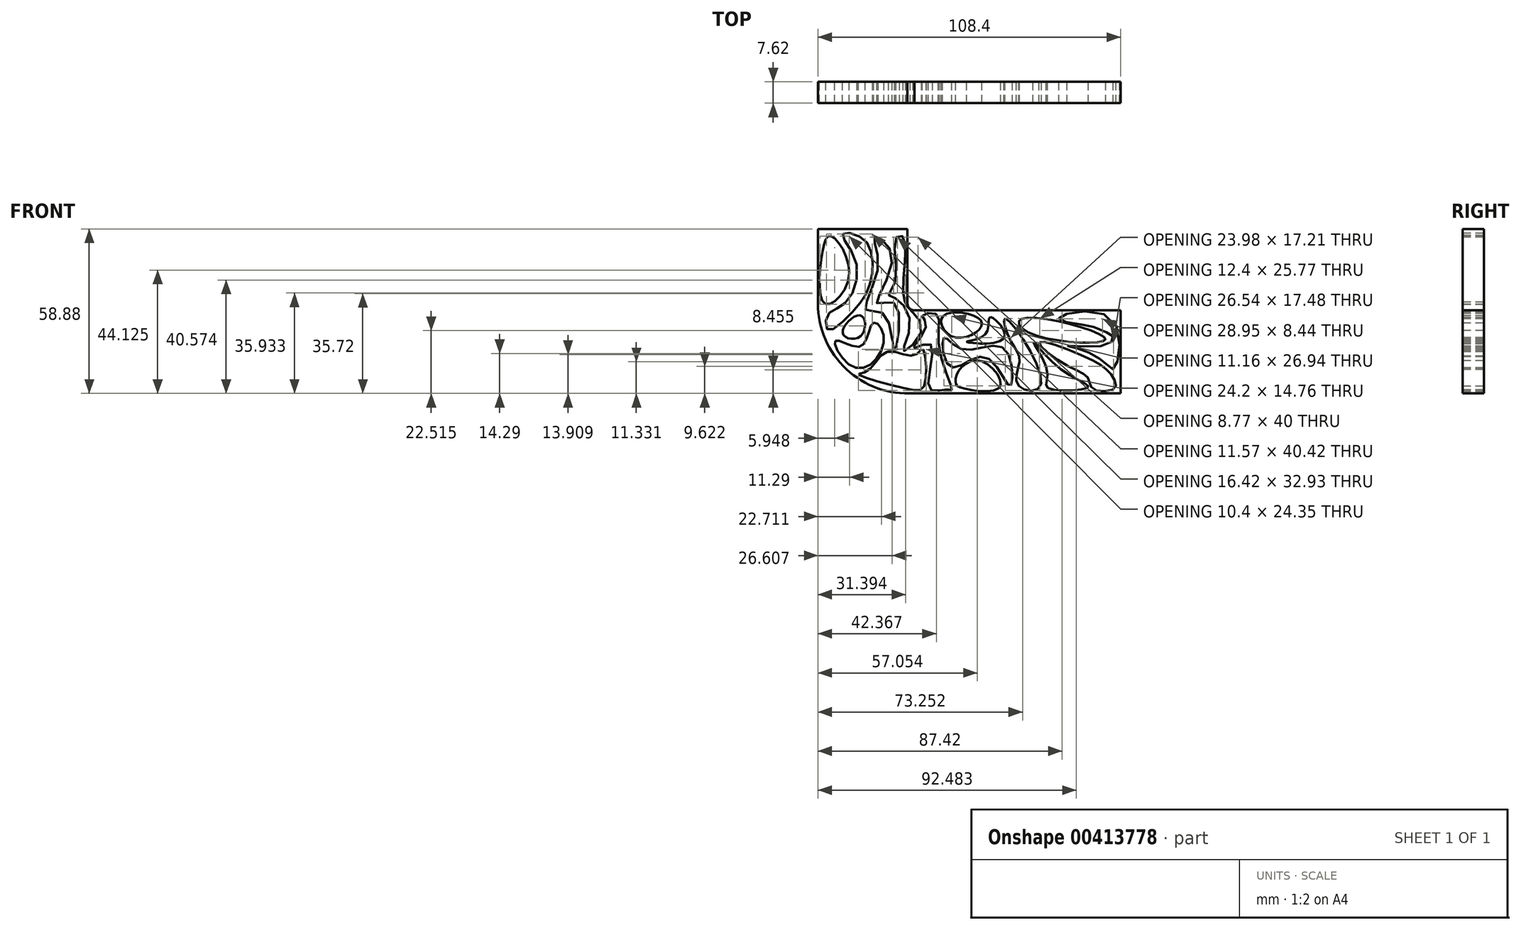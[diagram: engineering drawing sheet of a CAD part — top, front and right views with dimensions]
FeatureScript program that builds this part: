
annotation { "Feature Type Name" : "Feature", "Feature Type Description" : "" }
export const myFeature = defineFeature(function(context is Context, id is Id, definition is map)
    precondition{}
    {
        {
            var Q0;
            Q0=qCreatedBy(makeId("Front.planeOp"),FACE);
            var sketch = newSketch(context, id + "F0", { "sketchPlane" : qUnion([Q0])});
            skLineSegment(sketch, "E0", {"start": v(-56.41, 26.73) * mm, "end": v(-56.41, 0) * mm});
            skLineSegment(sketch, "E1", {"start": v(-56.41, 26.73) * mm, "end": v(-24.33, 26.73) * mm});
            skLineSegment(sketch, "E2", {"start": v(-24.33, 26.73) * mm, "end": v(-24.33, 0) * mm});
            skArc(sketch, "E3", {"start": v(-56.41, 0) * mm, "mid": v(-46.23, -23.48) * mm, "end": v(-22.12, -32.08) * mm});
            skArc(sketch, "E4", {"start": v(-24.33, 0) * mm, "mid": v(-23.58, -1.74) * mm, "end": v(-21.8, -2.4) * mm});
            skLineSegment(sketch, "E5", {"start": v(-21.8, -2.4) * mm, "end": v(25.07, -2.4) * mm});
            skLineSegment(sketch, "E6", {"start": v(25.07, -2.4) * mm, "end": v(51.99, -2.4) * mm});
            skLineSegment(sketch, "E7", {"start": v(51.99, -2.4) * mm, "end": v(51.99, -32.08) * mm});
            skLineSegment(sketch, "E8", {"start": v(-22.12, -32.08) * mm, "end": v(51.99, -32.08) * mm});
            skFitSpline(sketch, "E9", {"points": [v(-51.8, 24.15) * mm, v(-54.75, 18.8) * mm, v(-53.83, 0) * mm, v(-45.35, 9.59) * mm, v(-51.8, 24.15) * mm]});
            skFitSpline(sketch, "E10", {"points": [v(-47.56, 24.89) * mm, v(-42.95, 15.49) * mm, v(-46.83, 0) * mm, v(-52.9, -4.06) * mm, v(-52.73, -9.4) * mm, v(-44.25, -3.13) * mm, v(-38.16, 5.72) * mm, v(-37.06, 16.96) * mm, v(-41.11, 23.78) * mm, v(-47.56, 24.89) * mm]});
            skFitSpline(sketch, "E11", {"points": [v(-50.14, -13.27) * mm, v(-42.77, -23.04) * mm, v(-32.82, -12.72) * mm, v(-36.69, -7) * mm, v(-41.11, -15.3) * mm, v(-50.14, -13.27) * mm]});
            skFitSpline(sketch, "E12", {"points": [v(-47.56, -10.5) * mm, v(-41.11, -11.61) * mm, v(-41.11, -4.24) * mm, v(-47.56, -10.5) * mm]});
            skFitSpline(sketch, "E13", {"points": [v(-36.13, 23.78) * mm, v(-34.84, 14.01) * mm, v(-39.27, -2.21) * mm, v(-32.63, -3.87) * mm, v(-28.94, -16.78) * mm, v(-28.76, 0) * mm, v(-35.21, 0) * mm, v(-29.87, 16.96) * mm, v(-36.13, 23.78) * mm]});
            skFitSpline(sketch, "E14", {"points": [v(-28.4, 23.78) * mm, v(-28.76, 7.74) * mm, v(-31.16, 3.13) * mm, v(-28.76, 2.03) * mm, v(-23.41, -7.74) * mm, v(-25.8, -16.96) * mm, v(-19.36, -9.59) * mm, v(-22.9, -2.72) * mm, v(-24.93, -0.14) * mm, v(-25.9, 7.47) * mm, v(-25.83, 23.78) * mm, v(-28.4, 23.78) * mm]});
            skFitSpline(sketch, "E15", {"points": [v(-31.62, -17.25) * mm, v(-38.78, -24.16) * mm, v(-41.95, -25.32) * mm, v(-23.42, -30.76) * mm, v(-18.23, -29) * mm, v(-18.86, -16.3) * mm, v(-21.8, -18.5) * mm, v(-31.62, -17.25) * mm]});
            skFitSpline(sketch, "E16", {"points": [v(-19.04, -4.4) * mm, v(-17.6, -7.78) * mm, v(-22.3, -16) * mm, v(-16.17, -14.56) * mm, v(-16.56, -30.46) * mm, v(-10.3, -30.72) * mm, v(-8.48, -30.86) * mm, v(-13.17, -14.82) * mm, v(-14.08, -3.74) * mm, v(-19.04, -4.4) * mm]});
            skFitSpline(sketch, "E17", {"points": [v(-11.6, -4.4) * mm, v(2.21, -6.6) * mm, v(-7.3, -12.08) * mm, v(-11.6, -4.4) * mm]});
            skFitSpline(sketch, "E18", {"points": [v(-11.35, -12.21) * mm, v(-9, -22.64) * mm, v(3.52, -19.12) * mm, v(12.38, -29.42) * mm, v(10.42, -16.3) * mm, v(-4.96, -16.3) * mm, v(-11.35, -12.21) * mm]});
            skFitSpline(sketch, "E19", {"points": [v(2.27, -20.65) * mm, v(-6.13, -24.16) * mm, v(-7.1, -28.49) * mm, v(-5.42, -30) * mm, v(8.64, -29.93) * mm, v(2.27, -20.65) * mm]});
            skFitSpline(sketch, "E20", {"points": [v(5.35, -4.87) * mm, v(3.57, -10.93) * mm, v(-3.12, -13.68) * mm, v(10.24, -12.29) * mm, v(5.35, -4.87) * mm]});
            skFitSpline(sketch, "E21", {"points": [v(10.64, -5.36) * mm, v(12.71, -13.53) * mm, v(15.76, -20.32) * mm, v(15.35, -29.35) * mm, v(23.39, -29.18) * mm, v(10.64, -5.36) * mm]});
            skFitSpline(sketch, "E22", {"points": [v(16.6, -5.42) * mm, v(46.52, -12.55) * mm, v(19.08, -10.38) * mm, v(16.6, -5.42) * mm]});
            skFitSpline(sketch, "E23", {"points": [v(20.64, -13.79) * mm, v(25.75, -24.95) * mm, v(25.9, -30.22) * mm, v(40.17, -30.06) * mm, v(31.95, -24.48) * mm, v(20.64, -13.79) * mm]});
            skFitSpline(sketch, "E24", {"points": [v(22.8, -13.79) * mm, v(32.73, -22.16) * mm, v(40.32, -26.65) * mm, v(41.87, -30.37) * mm, v(49.78, -30.37) * mm, v(48.7, -25.57) * mm, v(41.1, -19.99) * mm, v(22.8, -13.79) * mm]});
            skFitSpline(sketch, "E25", {"points": [v(29.79, -5.3) * mm, v(48.24, -5.16) * mm, v(49.53, -23.3) * mm, v(46.8, -21.6) * mm, v(36.58, -16.08) * mm, v(32.86, -15.08) * mm, v(47, -14.67) * mm, v(49.13, -11.67) * mm, v(45.07, -9.56) * mm, v(41.5, -8.16) * mm, v(29.79, -5.3) * mm]});
            skSolve(sketch);
        }
        {
            var Q0;
            Q0=makeQuery(id+"F0.imprint","IMPRINT",FACE,{"disambiguationData":[TD([[makeQuery(id+"F0.imprint","IMPRINT",EDGE,{"derivedFrom":sQuery(id+"F0.wireOp",EDGE,"E0")}),1.0]])]});
            extrude(context, id + "F1", {"entities" : qUnion([Q0]), "depth" : 7.62 * mm});
        }
    });
